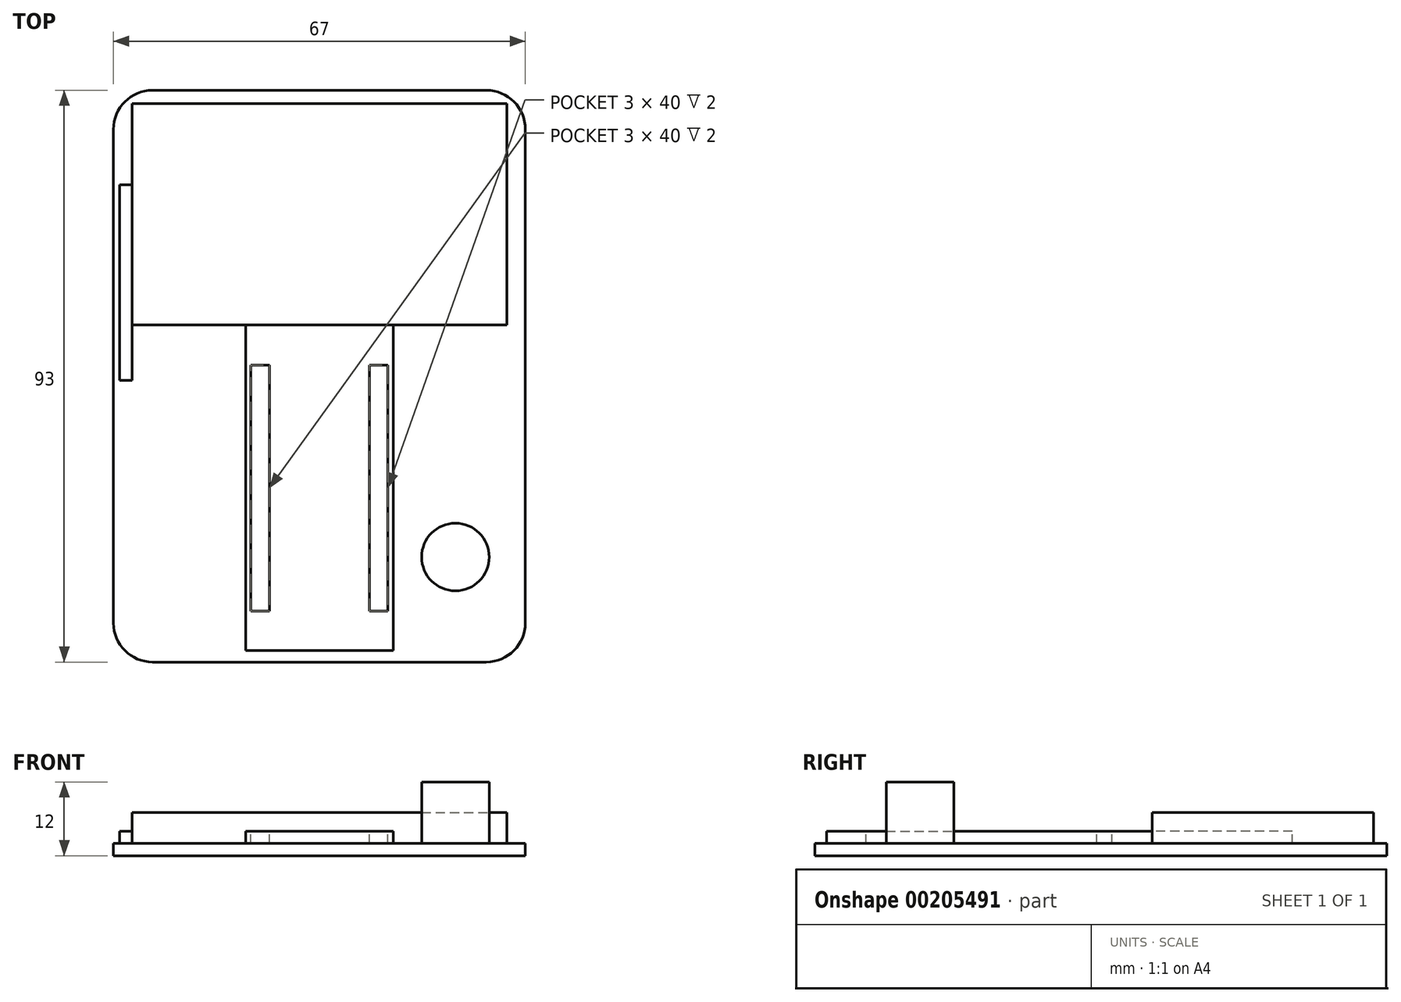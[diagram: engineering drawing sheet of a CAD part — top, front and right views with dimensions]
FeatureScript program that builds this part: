
annotation { "Feature Type Name" : "Feature", "Feature Type Description" : "" }
export const myFeature = defineFeature(function(context is Context, id is Id, definition is map)
    precondition{}
    {
        {
            var Q0;
            Q0=qCreatedBy(makeId("Top.planeOp"),FACE);
            var sketch = newSketch(context, id + "F0", { "sketchPlane" : qUnion([Q0])});
            skLineSegment(sketch, "E0.bottom", {"start": v(-27.15, 46.5) * mm, "end": v(27.15, 46.5) * mm});
            skLineSegment(sketch, "E0.top", {"start": v(-27.15, -46.5) * mm, "end": v(27.15, -46.5) * mm});
            skLineSegment(sketch, "E0.left", {"start": v(-33.5, 40.15) * mm, "end": v(-33.5, -40.15) * mm});
            skLineSegment(sketch, "E0.right", {"start": v(33.5, 40.15) * mm, "end": v(33.5, -40.15) * mm});
            skPoint(sketch, "E0.middle", {"position": v(0, 0) * mm});
            skPoint(sketch, "E1.visualSharp", {"position": v(-33.5, 46.5) * mm});
            skLineSegment(sketch, "E1.filletArc", {"start": v(-33.5, 46.5) * mm, "end": v(-33.5, 46.5) * mm});
            skPoint(sketch, "E2.visualSharp", {"position": v(33.5, 46.5) * mm});
            skLineSegment(sketch, "E2.filletArc", {"start": v(33.5, 46.5) * mm, "end": v(33.5, 46.5) * mm});
            skPoint(sketch, "E3.visualSharp", {"position": v(33.5, -46.5) * mm});
            skLineSegment(sketch, "E3.filletArc", {"start": v(33.5, -46.5) * mm, "end": v(33.5, -46.5) * mm});
            skPoint(sketch, "E4.visualSharp", {"position": v(-33.5, -46.5) * mm});
            skLineSegment(sketch, "E4.filletArc", {"start": v(-33.5, -46.5) * mm, "end": v(-33.5, -46.5) * mm});
            skPoint(sketch, "E5.middle", {"position": v(0, 25.08) * mm});
            skArc(sketch, "E6.filletArc", {"start": v(-33.5, -40.15) * mm, "mid": v(-31.64, -44.64) * mm, "end": v(-27.15, -46.5) * mm});
            skArc(sketch, "E7.filletArc", {"start": v(27.15, -46.5) * mm, "mid": v(31.64, -44.64) * mm, "end": v(33.5, -40.15) * mm});
            skArc(sketch, "E8.filletArc", {"start": v(-27.15, 46.5) * mm, "mid": v(-31.64, 44.64) * mm, "end": v(-33.5, 40.15) * mm});
            skArc(sketch, "E9.filletArc", {"start": v(33.5, 40.15) * mm, "mid": v(31.64, 44.64) * mm, "end": v(27.15, 46.5) * mm});
            skSolve(sketch);
        }
        {
            var Q0;
            Q0=makeQuery(id+"F0.imprint","IMPRINT",FACE,{"disambiguationData":[TD([[makeQuery(id+"F0.imprint","IMPRINT",EDGE,{"derivedFrom":sQuery(id+"F0.wireOp",EDGE,"E0.bottom")}),-1.0]])]});
            extrude(context, id + "F1", {"entities" : qUnion([Q0]), "depth" : 12 * mm});
        }
        {
            var Q0;
            Q0=makeQuery(id+"F1.opExtrude","CAP_FACE",FACE,{"disambiguationData":[OSD([sQuery(id+"F0.wireOp",EDGE,"E0.bottom"),sQuery(id+"F0.wireOp",EDGE,"E0.top"),sQuery(id+"F0.wireOp",EDGE,"E0.left"),sQuery(id+"F0.wireOp",EDGE,"E0.right"),sQuery(id+"F0.wireOp",EDGE,"E1.filletArc"),sQuery(id+"F0.wireOp",EDGE,"E2.filletArc"),sQuery(id+"F0.wireOp",EDGE,"E3.filletArc"),sQuery(id+"F0.wireOp",EDGE,"E4.filletArc")])],"isStart":false});
            var sketch = newSketch(context, id + "F2", { "sketchPlane" : qUnion([Q0])});
            skLineSegment(sketch, "E10.bottom", {"start": v(-30.5, 8.36) * mm, "end": v(30.5, 8.36) * mm});
            skLineSegment(sketch, "E10.top", {"start": v(-30.5, 44.36) * mm, "end": v(30.5, 44.36) * mm});
            skLineSegment(sketch, "E10.left", {"start": v(-30.5, 8.36) * mm, "end": v(-30.5, 44.36) * mm});
            skLineSegment(sketch, "E10.right", {"start": v(30.5, 8.36) * mm, "end": v(30.5, 44.36) * mm});
            skPoint(sketch, "E10.middle", {"position": v(0, 26.36) * mm});
            skLineSegment(sketch, "E11.bottom", {"start": v(-12, -44.64) * mm, "end": v(12, -44.64) * mm});
            skLineSegment(sketch, "E11.top", {"start": v(-12, 8.36) * mm, "end": v(12, 8.36) * mm});
            skLineSegment(sketch, "E11.left", {"start": v(-12, -44.64) * mm, "end": v(-12, 8.36) * mm});
            skLineSegment(sketch, "E11.right", {"start": v(12, -44.64) * mm, "end": v(12, 8.36) * mm});
            skPoint(sketch, "E11.middle", {"position": v(0, -18.14) * mm});
            skLineSegment(sketch, "E12", {"start": v(-33.5, 31.16) * mm, "end": v(-32.5, 31.16) * mm});
            skLineSegment(sketch, "E13", {"start": v(-32.5, 31.16) * mm, "end": v(-30.5, 31.16) * mm});
            skLineSegment(sketch, "E14.top", {"start": v(-32.5, -0.7) * mm, "end": v(-30.5, -0.7) * mm});
            skLineSegment(sketch, "E14.left", {"start": v(-32.5, 31.16) * mm, "end": v(-32.5, -0.7) * mm});
            skLineSegment(sketch, "E14.right", {"start": v(-30.5, 31.16) * mm, "end": v(-30.5, -0.7) * mm});
            skCircle(sketch, "E15", {"center": v(-22.12, -29.42) * mm, "radius": 5.5 * mm});
            skCircle(sketch, "E16.MirrorC", {"center": v(22.12, -29.42) * mm, "radius": 5.5 * mm});
            skLineSegment(sketch, "E17", {"start": v(23.36, -24.06) * mm, "end": v(23.36, -19.9) * mm});
            skLineSegment(sketch, "E18", {"start": v(23.36, -19.9) * mm, "end": v(19.58, -19.9) * mm});
            skLineSegment(sketch, "E19", {"start": v(19.58, -19.9) * mm, "end": v(19.58, -24.55) * mm});
            skLineSegment(sketch, "E20.MirrorCS", {"start": v(-19.58, -19.9) * mm, "end": v(-19.58, -24.55) * mm});
            skLineSegment(sketch, "E21.MirrorCS", {"start": v(-23.36, -19.9) * mm, "end": v(-19.58, -19.9) * mm});
            skLineSegment(sketch, "E22.MirrorCS", {"start": v(-23.36, -24.06) * mm, "end": v(-23.36, -19.9) * mm});
            skSolve(sketch);
        }
        {
            var Q0;
            Q0=makeQuery(id+"F2.imprint","IMPRINT",FACE,{"disambiguationData":[TD([[makeQuery(id+"F2.imprint","IMPRINT",EDGE,{"derivedFrom":sQuery(id+"F2.wireOp",EDGE,"E10.top")}),-1.0]])]});
            extrude(context, id + "F3", {"entities" : qUnion([Q0]), "operationType" : NewBodyOperationType.REMOVE, "oppositeDirection" : true, "depth" : 5 * mm});
        }
        {
            var Q0;
            Q0=makeQuery(id+"F2.imprint","IMPRINT",FACE,{"disambiguationData":[TD([[makeQuery(id+"F2.imprint","IMPRINT",EDGE,{"derivedFrom":sQuery(id+"F2.wireOp",EDGE,"E10.top")}),1.0]])]});
            var sketch = newSketch(context, id + "F4", { "sketchPlane" : qUnion([Q0])});
            skLineSegment(sketch, "E23", {"start": v(-30.5, 7.03) * mm, "end": v(-30.5, -44.47) * mm});
            skLineSegment(sketch, "E24", {"start": v(-30.5, -44.47) * mm, "end": v(30.23, -44.47) * mm});
            skLineSegment(sketch, "E25", {"start": v(30.23, -44.47) * mm, "end": v(30.23, 6.94) * mm});
            skLineSegment(sketch, "E26", {"start": v(-30.5, 7.03) * mm, "end": v(30.23, 6.94) * mm});
            skLineSegment(sketch, "E27", {"start": v(-32.5, -0.7) * mm, "end": v(-30.5, -0.7) * mm});
            skLineSegment(sketch, "E28", {"start": v(-30.5, 8.36) * mm, "end": v(-30.5, 7.03) * mm});
            skLineSegment(sketch, "E29", {"start": v(-20, 7.01) * mm, "end": v(-20, 7.38) * mm});
            skLineSegment(sketch, "E30", {"start": v(19.64, 6.95) * mm, "end": v(19.64, 8.35) * mm});
            skSolve(sketch);
        }
        {
            var Q0;
            {var subQ5=sQuery(id+"F4.wireOp",EDGE,"E23");Q0=makeQuery(id+"F4.imprint","IMPRINT",FACE,{"disambiguationData":[TD([[makeQuery(id+"F4.imprint","IMPRINT",EDGE,{"derivedFrom":subQ5}),1.0]])]});}
            var Q1;
            {var subQ0=sQuery(id+"F4.wireOp",EDGE,"E25");Q1=makeQuery(id+"F4.imprint","IMPRINT",FACE,{"disambiguationData":[TD([[makeQuery(id+"F4.imprint","IMPRINT",EDGE,{"derivedFrom":subQ0}),1.0]])]});}
            var Q2;
            Q2=makeQuery(id+"F2.imprint","IMPRINT",FACE,{"disambiguationData":[TD([[makeQuery(id+"F2.imprint","IMPRINT",EDGE,{"derivedFrom":sQuery(id+"F2.wireOp",EDGE,"E11.bottom")}),1.0]])]});
            var Q3;
            {var subQ2=sQuery(id+"F2.wireOp",EDGE,"E13");Q3=makeQuery(id+"F2.imprint","IMPRINT",FACE,{"disambiguationData":[TD([[makeQuery(id+"F2.imprint","IMPRINT",EDGE,{"derivedFrom":subQ2}),-1.0]])]});}
            var Q4;
            {var subQ1=sQuery(id+"F4.wireOp",EDGE,"E23");var subQ8=sQuery(id+"F4.wireOp",EDGE,"E27");var subQ12=makeQuery(id+"F4.imprint","INTERSECT",VERTEX,{"derivedFrom":[subQ1,subQ8]});Q4=makeQuery(id+"F4.imprint","IMPRINT",FACE,{"disambiguationData":[TD([[makeQuery(id+"F4.imprint","IMPRINT",EDGE,{"disambiguationData":[TD([[subQ12,1.0]])],"derivedFrom":subQ8}),1.0]])]});}
            var Q5;
            {var subQ0=sQuery(id+"F2.wireOp",EDGE,"E20.MirrorCS");Q5=makeQuery(id+"F2.imprint","IMPRINT",FACE,{"disambiguationData":[TD([[makeQuery(id+"F2.imprint","IMPRINT",EDGE,{"derivedFrom":subQ0}),-1.0]])]});}
            var Q6;
            {var subQ0=sQuery(id+"F2.wireOp",EDGE,"E17");Q6=makeQuery(id+"F2.imprint","IMPRINT",FACE,{"disambiguationData":[TD([[makeQuery(id+"F2.imprint","IMPRINT",EDGE,{"derivedFrom":subQ0}),1.0]])]});}
            extrude(context, id + "F5", {"entities" : qUnion([Q0, Q1, Q2, Q3, Q4, Q5, Q6]), "operationType" : NewBodyOperationType.REMOVE, "oppositeDirection" : true, "depth" : 8 * mm});
        }
        {
            var Q0;
            Q0=makeQuery(id+"F2.imprint","IMPRINT",FACE,{"disambiguationData":[TD([[makeQuery(id+"F2.imprint","IMPRINT",EDGE,{"derivedFrom":sQuery(id+"F2.wireOp",EDGE,"E15")}),1.0]])]});
            var Q1;
            Q1=makeQuery(id+"F2.imprint","IMPRINT",FACE,{"disambiguationData":[TD([[makeQuery(id+"F2.imprint","IMPRINT",EDGE,{"derivedFrom":sQuery(id+"F2.wireOp",EDGE,"E16.MirrorC")}),-1.0]])]});
            extrude(context, id + "F6", {"entities" : qUnion([Q0, Q1]), "operationType" : NewBodyOperationType.REMOVE, "oppositeDirection" : true, "depth" : 10 * mm});
        }
        {
            var Q0;
            {var subQ0=sQuery(id+"F4.wireOp",EDGE,"E24");var subQ1=makeQuery(id+"F2.imprint","IMPRINT",EDGE,{"derivedFrom":sQuery(id+"F2.wireOp",EDGE,"E11.left")});var subQ2=makeQuery(id+"F4.imprint","INTERSECT",VERTEX,{"derivedFrom":[subQ1,subQ0]});Q0=makeQuery(id+"F4.imprint","IMPRINT",FACE,{"disambiguationData":[TD([[makeQuery(id+"F4.imprint","IMPRINT",EDGE,{"disambiguationData":[TD([[subQ2,-1.0]])],"derivedFrom":subQ0}),1.0]])]});}
            var sketch = newSketch(context, id + "F7", { "sketchPlane" : qUnion([Q0])});
            skLineSegment(sketch, "E31.bottom", {"start": v(-11.14, -38.21) * mm, "end": v(-8.14, -38.21) * mm});
            skLineSegment(sketch, "E31.top", {"start": v(-11.14, 1.79) * mm, "end": v(-8.14, 1.79) * mm});
            skLineSegment(sketch, "E31.left", {"start": v(-11.14, -38.21) * mm, "end": v(-11.14, 1.79) * mm});
            skLineSegment(sketch, "E31.right", {"start": v(-8.14, -38.21) * mm, "end": v(-8.14, 1.79) * mm});
            skLineSegment(sketch, "E32", {"start": v(-8.14, -38.21) * mm, "end": v(9.86, -38.21) * mm});
            skLineSegment(sketch, "E33.MirrorCS", {"start": v(8.14, -38.21) * mm, "end": v(8.14, 1.79) * mm});
            skLineSegment(sketch, "E34.MirrorCS", {"start": v(11.14, -38.21) * mm, "end": v(11.14, 1.79) * mm});
            skLineSegment(sketch, "E35.MirrorCS", {"start": v(11.14, 1.79) * mm, "end": v(8.14, 1.79) * mm});
            skLineSegment(sketch, "E36", {"start": v(9.86, -38.21) * mm, "end": v(11.14, -38.21) * mm});
            skLineSegment(sketch, "E37", {"start": v(-8.14, 1.79) * mm, "end": v(-8.14, 8.33) * mm});
            skLineSegment(sketch, "E38", {"start": v(-8.14, -38.21) * mm, "end": v(-8.14, -44.54) * mm});
            skSolve(sketch);
        }
        {
            var Q0;
            Q0=makeQuery(id+"F7.imprint","IMPRINT",FACE,{"disambiguationData":[TD([[makeQuery(id+"F7.imprint","IMPRINT",EDGE,{"derivedFrom":sQuery(id+"F7.wireOp",EDGE,"E31.bottom")}),1.0]])]});
            var Q1;
            {var subQ0=sQuery(id+"F7.wireOp",EDGE,"E33.MirrorCS");Q1=makeQuery(id+"F7.imprint","IMPRINT",FACE,{"disambiguationData":[TD([[makeQuery(id+"F7.imprint","IMPRINT",EDGE,{"derivedFrom":subQ0}),-1.0]])]});}
            extrude(context, id + "F8", {"entities" : qUnion([Q0, Q1]), "operationType" : NewBodyOperationType.REMOVE, "oppositeDirection" : true, "depth" : 10 * mm});
        }
        {
            var Q0;
            {var subQ0=sQuery(id+"F2.wireOp",EDGE,"E20.MirrorCS");Q0=makeQuery(id+"F4.imprint","IMPRINT",FACE,{"disambiguationData":[TD([[makeQuery(id+"F4.imprint","IMPRINT",EDGE,{"derivedFrom":makeQuery(id+"F2.imprint","IMPRINT",EDGE,{"derivedFrom":subQ0})}),-1.0]])]});}
            var Q1;
            {var subQ0=sQuery(id+"F2.wireOp",EDGE,"E16.MirrorC");var subQ1=makeQuery(id+"F2.imprint","INTERSECT",VERTEX,{"derivedFrom":[subQ0,sQuery(id+"F2.wireOp",EDGE,"E17")]});Q1=makeQuery(id+"F2.imprint","IMPRINT",FACE,{"disambiguationData":[TD([[makeQuery(id+"F2.imprint","IMPRINT",EDGE,{"disambiguationData":[TD([[subQ1,1.0]])],"derivedFrom":subQ0}),-1.0]])]});}
            var Q2;
            {var subQ0=sQuery(id+"F2.wireOp",EDGE,"E17");Q2=makeQuery(id+"F2.imprint","IMPRINT",FACE,{"disambiguationData":[TD([[makeQuery(id+"F2.imprint","IMPRINT",EDGE,{"derivedFrom":subQ0}),1.0]])]});}
            extrude(context, id + "F9", {"entities" : qUnion([Q0, Q1, Q2]), "operationType" : NewBodyOperationType.REMOVE, "oppositeDirection" : true, "depth" : 10 * mm});
        }
    });
